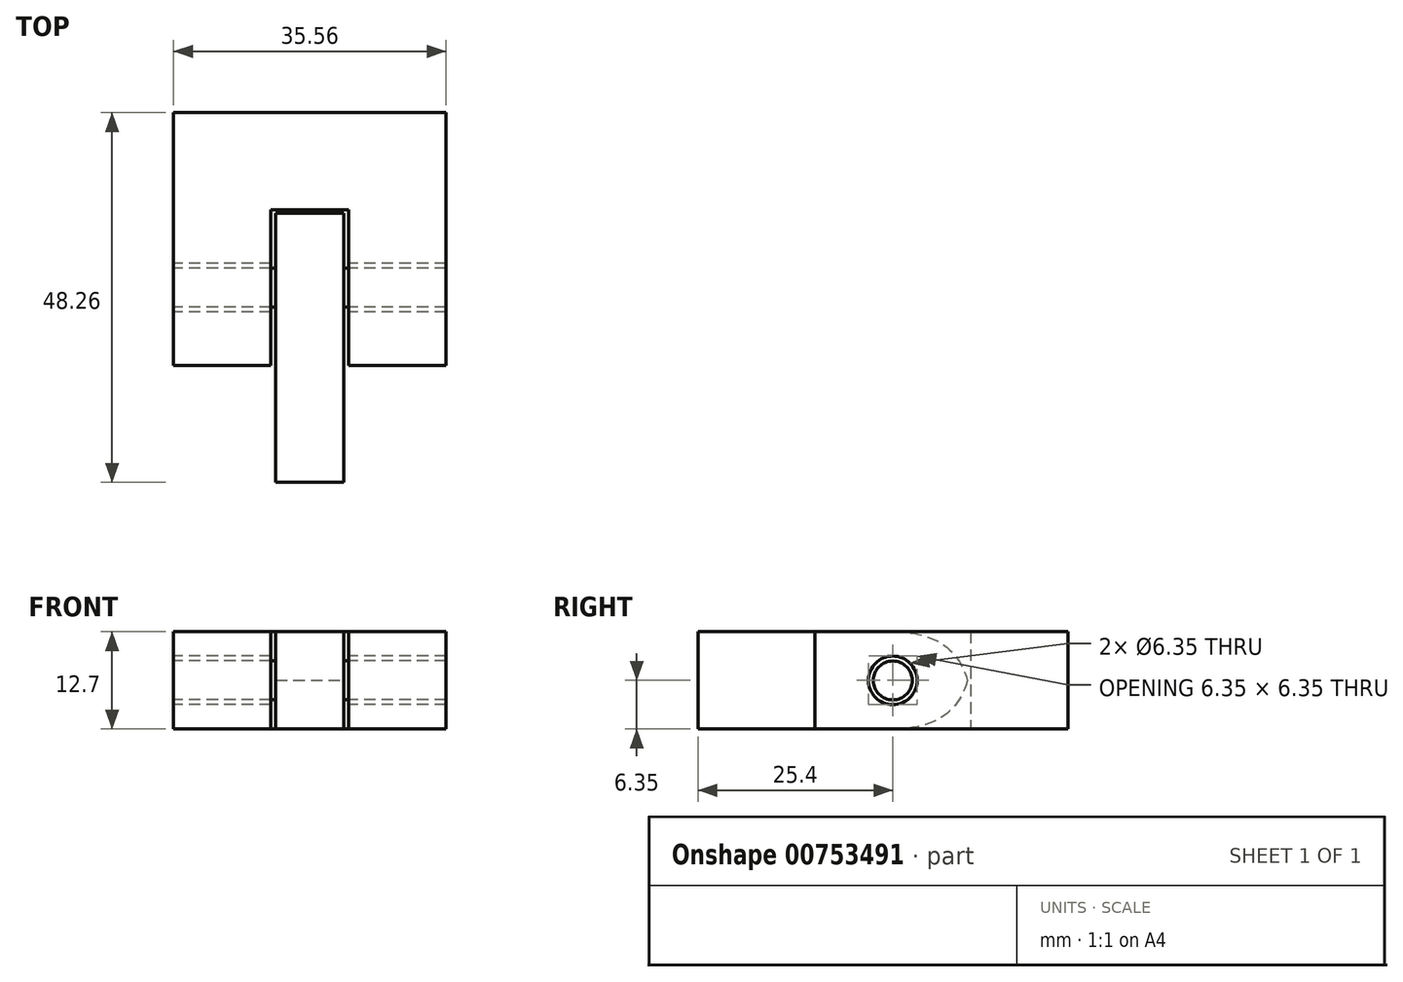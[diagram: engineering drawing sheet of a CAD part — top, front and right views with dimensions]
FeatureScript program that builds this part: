
annotation { "Feature Type Name" : "Feature", "Feature Type Description" : "" }
export const myFeature = defineFeature(function(context is Context, id is Id, definition is map)
    precondition{}
    {
        {
            var Q0;
            Q0=qCreatedBy(makeId("Top.planeOp"),FACE);
            var sketch = newSketch(context, id + "F0", { "sketchPlane" : qUnion([Q0])});
            skLineSegment(sketch, "E0", {"start": v(0, 0) * mm, "end": v(-10.16, 0) * mm});
            skLineSegment(sketch, "E1", {"start": v(-10.16, 0) * mm, "end": v(-10.16, -20.32) * mm});
            skLineSegment(sketch, "E2", {"start": v(-10.16, -20.32) * mm, "end": v(-22.86, -20.32) * mm});
            skLineSegment(sketch, "E3", {"start": v(-22.86, -20.32) * mm, "end": v(-22.86, 12.7) * mm});
            skLineSegment(sketch, "E4", {"start": v(-22.86, 12.7) * mm, "end": v(12.7, 12.7) * mm});
            skLineSegment(sketch, "E5", {"start": v(12.7, 12.7) * mm, "end": v(12.7, -20.32) * mm});
            skLineSegment(sketch, "E6", {"start": v(12.7, -20.32) * mm, "end": v(0, -20.32) * mm});
            skLineSegment(sketch, "E7", {"start": v(0, -20.32) * mm, "end": v(0, 0) * mm});
            skSolve(sketch);
        }
        {
            var Q0;
            Q0=makeQuery(id+"F0.imprint","IMPRINT",FACE,{"disambiguationData":[TD([[makeQuery(id+"F0.imprint","IMPRINT",EDGE,{"derivedFrom":sQuery(id+"F0.wireOp",EDGE,"E0")}),-1.0]])]});
            extrude(context, id + "F1", {"entities" : qUnion([Q0]), "depth" : 12.7 * mm, "offsetDistance" : 25.4 * mm});
        }
        {
            var Q0;
            Q0=makeQuery(id+"F1.opExtrude","SWEPT_FACE",FACE,{"disambiguationData":[OSD([sQuery(id+"F0.wireOp",EDGE,"E3")])]});
            var sketch = newSketch(context, id + "F2", { "sketchPlane" : qUnion([Q0])});
            skCircle(sketch, "E8", {"center": v(10.16, 6.35) * mm, "radius": 3.18 * mm});
            skSolve(sketch);
        }
        {
            var Q0;
            Q0=makeQuery(id+"F2.imprint","IMPRINT",FACE,{"disambiguationData":[TD([[makeQuery(id+"F2.imprint","IMPRINT",EDGE,{"derivedFrom":sQuery(id+"F2.wireOp",EDGE,"E8")}),1.0]])]});
            extrude(context, id + "F3", {"entities" : qUnion([Q0]), "operationType" : NewBodyOperationType.REMOVE, "oppositeDirection" : true, "depth" : 50.8 * mm, "offsetDistance" : 25.4 * mm});
        }
        {
            var Q0;
            Q0=qCreatedBy(makeId("Top.planeOp"),FACE);
            var sketch = newSketch(context, id + "F4", { "sketchPlane" : qUnion([Q0])});
            skLineSegment(sketch, "E9", {"start": v(-9.53, 0) * mm, "end": v(-9.52, -35.56) * mm});
            skLineSegment(sketch, "E10", {"start": v(-9.52, -35.56) * mm, "end": v(-0.63, -35.56) * mm});
            skLineSegment(sketch, "E11", {"start": v(-0.63, -35.56) * mm, "end": v(-0.64, 0) * mm});
            skLineSegment(sketch, "E12", {"start": v(-0.64, 0) * mm, "end": v(-9.53, 0) * mm});
            skSolve(sketch);
        }
        {
            var Q0;
            Q0=makeQuery(id+"F4.imprint","IMPRINT",FACE,{"disambiguationData":[TD([[makeQuery(id+"F4.imprint","IMPRINT",EDGE,{"derivedFrom":sQuery(id+"F4.wireOp",EDGE,"E9")}),1.0]])]});
            extrude(context, id + "F5", {"entities" : qUnion([Q0]), "depth" : 12.7 * mm, "offsetDistance" : 25.4 * mm});
        }
        {
            var Q0;
            Q0=makeQuery(id+"F1.opExtrude","SWEPT_FACE",FACE,{"disambiguationData":[OSD([sQuery(id+"F0.wireOp",EDGE,"E3")])]});
            var sketch = newSketch(context, id + "F6", { "sketchPlane" : qUnion([Q0])});
            skCircle(sketch, "E13", {"center": v(10.16, 6.35) * mm, "radius": 2.54 * mm});
            skSolve(sketch);
        }
        {
            var Q0;
            Q0=makeQuery(id+"F6.imprint","IMPRINT",FACE,{"disambiguationData":[TD([[makeQuery(id+"F6.imprint","IMPRINT",EDGE,{"derivedFrom":sQuery(id+"F6.wireOp",EDGE,"E13")}),1.0]])]});
            extrude(context, id + "F7", {"entities" : qUnion([Q0]), "operationType" : NewBodyOperationType.ADD, "oppositeDirection" : true, "depth" : 35.56 * mm, "offsetDistance" : 25.4 * mm});
        }
        {
            var Q0;
            Q0=makeQuery(id+"F5.opExtrude","CAP_EDGE",EDGE,{"disambiguationData":[OSD([sQuery(id+"F4.wireOp",EDGE,"E12")])],"isStart":false});
            var Q1;
            Q1=makeQuery(id+"F5.opExtrude","CAP_EDGE",EDGE,{"disambiguationData":[OSD([sQuery(id+"F4.wireOp",EDGE,"E12")])],"isStart":true});
            fillet(context, id + "F8", {"entities" : qUnion([Q0, Q1]), "radius" : 10.16 * mm, "tangentPropagation" : true, "rho" : 0.5, "crossSection" : FilletCrossSection.CONIC, "allowEdgeOverflow" : false});
        }
    });
